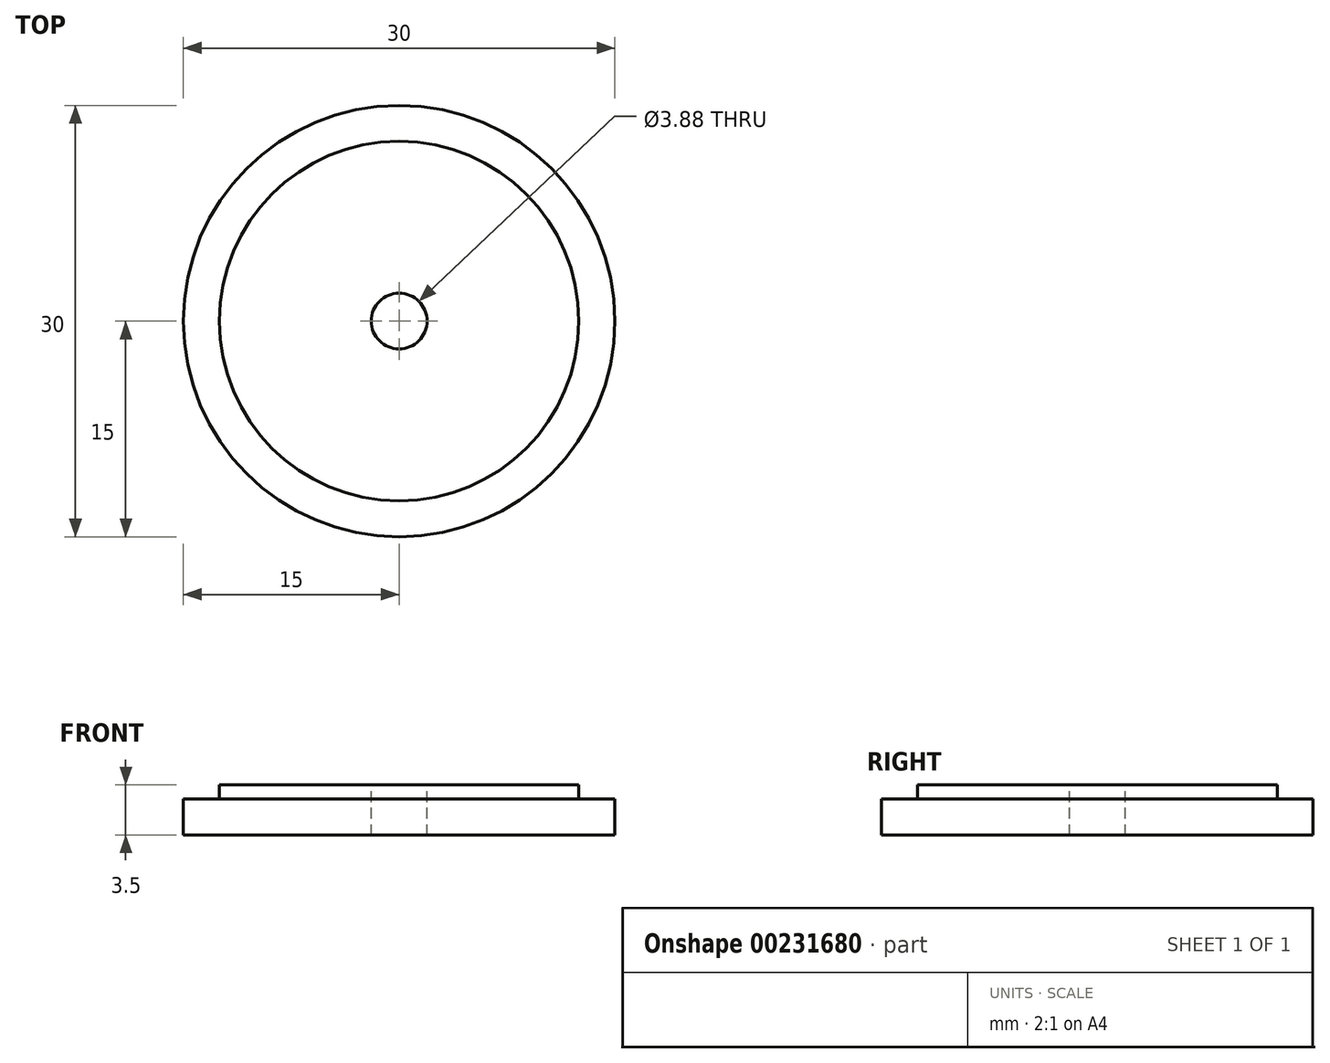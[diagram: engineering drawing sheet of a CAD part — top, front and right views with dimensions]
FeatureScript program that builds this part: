
annotation { "Feature Type Name" : "Feature", "Feature Type Description" : "" }
export const myFeature = defineFeature(function(context is Context, id is Id, definition is map)
    precondition{}
    {
        {
            var Q0;
            Q0=qCreatedBy(makeId("Top.planeOp"),FACE);
            var sketch = newSketch(context, id + "F0", { "sketchPlane" : qUnion([Q0])});
            skCircle(sketch, "E0", {"center": v(0, 0) * mm, "radius": 15 * mm});
            skSolve(sketch);
        }
        {
            var Q0;
            Q0 = qSketchRegion(id + "F0", true);
            extrude(context, id + "F1", {"entities" : qUnion([Q0]), "depth" : 2.5 * mm});
        }
        {
            var Q0;
            Q0=makeQuery(id+"F1.opExtrude","CAP_FACE",FACE,{"disambiguationData":[OSD([sQuery(id+"F0.wireOp",EDGE,"E0")])],"isStart":false});
            var sketch = newSketch(context, id + "F2", { "sketchPlane" : qUnion([Q0])});
            skCircle(sketch, "E1", {"center": v(0, 0) * mm, "radius": 12.5 * mm});
            skSolve(sketch);
        }
        {
            var Q0;
            Q0=makeQuery(id+"F2.imprint","IMPRINT",FACE,{"disambiguationData":[TD([[makeQuery(id+"F2.imprint","IMPRINT",EDGE,{"derivedFrom":sQuery(id+"F2.wireOp",EDGE,"E1")}),1.0]])]});
            extrude(context, id + "F3", {"entities" : qUnion([Q0]), "operationType" : NewBodyOperationType.ADD, "depth" : 1 * mm});
        }
        {
            var Q0;
            Q0=makeQuery(id+"F3.opExtrude","CAP_FACE",FACE,{"disambiguationData":[OSD([sQuery(id+"F2.wireOp",EDGE,"E1")])],"isStart":false});
            var sketch = newSketch(context, id + "F4", { "sketchPlane" : qUnion([Q0])});
            skCircle(sketch, "E2", {"center": v(0, 0) * mm, "radius": 1.94 * mm});
            skSolve(sketch);
        }
        {
            var Q0;
            Q0 = qSketchRegion(id + "F4", true);
            extrude(context, id + "F5", {"entities" : qUnion([Q0]), "operationType" : NewBodyOperationType.REMOVE, "endBound" : BoundingType.UP_TO_NEXT, "oppositeDirection" : true, "depth" : 25 * mm});
        }
    });
